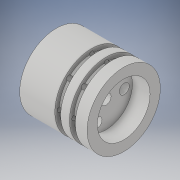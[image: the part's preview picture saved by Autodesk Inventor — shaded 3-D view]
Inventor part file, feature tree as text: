
AUTODESK INVENTOR PART (.ipt)
format: ipt  version: 2019 (Build 230136000, 136)  size: 250,880 bytes
history: native  units: in
note: dims shown in document units (in); Inventor stores cm internally (conversion verified against a paired STEP export)
features: sketch x8, extrude x7, hole x1
ambient origin geometry x8: Origin, YZ Plane, XZ Plane, XY Plane, X Axis, Y Axis, Z Axis, Center Point
bodies: Solid1 (feature_tree)
feature tree (16):
  extrude  "Extrusion1"  Depth=0.8661in
  extrude  "Extrusion2"  Depth=0.2559in
  extrude  "Extrusion3"  Depth=0.0787in TaperAngle=0.0deg
  extrude  "Extrusion4"  Depth=0.0787in TaperAngle=0.0deg
  extrude  "Extrusion5"  Depth=0.2441in
  hole  "Hole1"  [1 undecoded]
  extrude  "Extrusion9"  Depth=0.2362in
  extrude  "Extrusion10"  Depth=0.2362in
  sketch  "Sketch1"  dims[d0=0.9843in d1=0.8661in]
  sketch  "Sketch2"  dims[d2=0.2559in d3=0.0in d4=0.7087in]
  sketch  "Sketch3"  dims[d5=0.2165in d6=0.0in d7=0.0787in d8=0.0in]
  sketch  "Sketch4"  dims[d9=0.1181in d10=0.0in d11=0.0787in d12=0.0in]
  sketch  "Sketch5"  dims[d15=0.2441in d16=0.2441in]
  sketch  "Sketch7"  dims[d17=120.0deg d18=0.2441in]
  sketch  "Sketch10"  dims[d19=120.0deg]
  sketch  "Sketch11"  dims[d20=0.1339in d21=0.75in d22=0.248in d23=0.25in d24=90.0deg d25=1.0in d26=0.8108in d54=0.8661in d55=0.8661in d60=0.0591in d61=0.0591in d62=0.0591in d63=0.0591in d66=0.4331in d67=45.0deg d68=0.0591in d69=0.4331in d70=0.4331in d71=0.4331in d72=0.0591in d73=0.0591in d74=0.0591in d77=0.7087in d78=0.9843in d79=0.1575in d80=0.0in d81=0.0591in d82=0.0591in d83=0.1181in d84=0.2362in d85=0.0in d86=0.0in]
note: 1 required parameter value undecoded (feature->parameter linkage not recoverable at this tier; creation-order binding heuristic only, values carry confidence <= 0.55)
